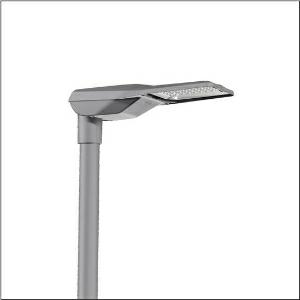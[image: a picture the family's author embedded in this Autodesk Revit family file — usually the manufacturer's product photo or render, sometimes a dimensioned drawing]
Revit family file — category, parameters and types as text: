
# Revit family: streetlight_sl_21_iq_mini___stw1_0a_5xe2e41d08jb_35ba
name_source: partatom
category: Lighting Fixtures
units: mm (PartAtom-declared; Revit-internal decimal feet)

## family parameters
Cut with Voids When Loaded = No
Host = Face
Light Source = No
Part Type = Normal
Room Calculation Point = No
Round Connector Dimension = Use Diameter
Shared = No

## types (1)
- --- (1 x LED, 11290 lm, 71.6 W, 4000K)
    Apparent Load = 72 VA
    CIE Flux Codes = 39 75 98 100 100
    Color Rendering = 70
    Color Temperature = 4000K
    Default Elevation = 1800 mm
    Description = Streetlight SL 21 iQ mini, mast luminaire, primary light control with lens, of PMMA, primary optical cover: cover, of toughened safety glass, transparent, light distribution: STW1.0a, light emission: direct distribution, primary light characteristic: asymmetric, installation type: post-top, side-entry, LED, High Power LED, rated luminous flux: 11.290lm, luminous efficacy: 158lm/W, light colour: 740, colour temperature: 4000K, control gear: iQ-Comfort, control: Auto-Match, Temp-Guard, Lumen-Switch, Night-Set, Smart-Wire, Light-Fading, Desk-Remote (wireless, voltage-free reading and setting of iQ features in the workshop via application-optimized NFC function/RFID function), optimised constant luminous flux control (CLO 2.0), pre-setting: linear dimming characteristic, mains connection: 220..240V, AC, 50/60Hz, start of lifetime: 72W, end of service life: 75W, reduction: 33W, luminaire housing, of diecast aluminium, powder-coated, SITECO metallic grey (DB 702S), corrosivity category C5 high according to DIN EN ISO 12944, please order mast flange separately, inclination adjustable: 0°, 5°, 10°, 15°, sealing non-destructively replaceable, multi-level sealing system, length: 628mm, width: 235mm, height: 110mm, mast flange for spigot size: 42mm (side-entry): 5XC10008XM4, 60/48mm (side-entry/post-top): 5XC10108XM2, 76/60mm (side-entry/post-top): 5XC10108XM1, mounting height: 4..8m, protection rating (complete): IP66, insulation class (complete): insulation class II (safety insulation), certification: CE, ENEC, ENEC+, VDE, impact resistance: IK10, permissible operating ambient temperature for outdoor applications: -40..+50°C, standard-compliant lighting for roads and squares, packaging unit: 1 piece

Light Distribution: STW1.0a
    Height = 110 mm
    Lamp = 1 x LED
    Lamp Light Flux = 11290 lm
    Lamp Power = 71.6 W
    Lamp count = 1
    Length = 625 mm
    Luminous efficacy = 158 lm/W
    Manufacturer = Siteco
    ModVariant = No
    Model = 5XE2E41D08JB
    Number of Poles = 1
    OnlyDefault = Yes
    Power Factor = 1
    Product Name = Streetlight SL 21 iQ mini | STW1.0a
    Product group = mast luminaire | pylon top
    ProductGroupID = 6100
    Protection Class = Protection class II
    Protection Degree = IP 66
    RLX_Detail_Level = 1
    RLX_Emergency_Light_Flux = 0 lm
    RLX_Emergency_Type = 0
    RLX_Emergency_Type_DB = No
    RlxData = <blob elided: 26453 chars, md5=d26d409e>
    Socket = socket
    Standby Power = 0 W
    System Light Flux = 11290 lm
    System Power = 72 W
    Type Comments = factory setting: luminous flux: 100 % | dim-lin: 254 | 746 mA
    Type Image = l_1003519.jpg
    URL = http://relux.com
    VarID = @adj_169635
    Voltage = 0 V
    Weight = 0.00 kg
    Width = 234 mm

## geometry (parser evidence)
native form markers: Blend x4, Sweep x10
no freeform markers — native parametric forms only
